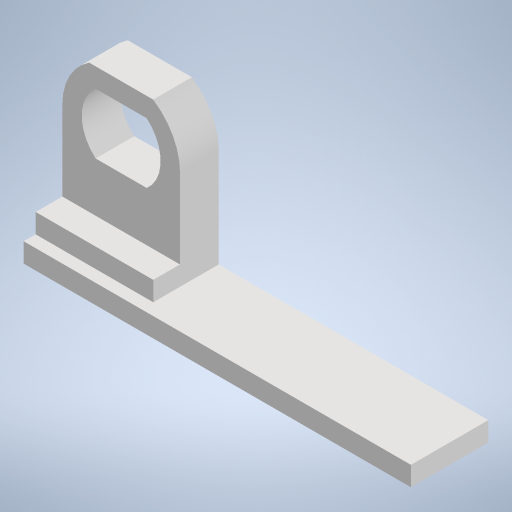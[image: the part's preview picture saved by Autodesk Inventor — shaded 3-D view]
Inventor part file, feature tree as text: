
AUTODESK INVENTOR PART (.ipt)
format: ipt  version: 2023 (Build 270158000, 158)  size: 253,440 bytes
history: native  units: mm
features: extrude x3, plane x2, sketch x1
ambient origin geometry x8: Origin, YZ Plane, XZ Plane, XY Plane, X Axis, Y Axis, Z Axis, Center Point
bodies: Solid1 (feature_tree)
feature tree (6):
  plane  "Work Plane1"
  sketch  "Sketch2"  dims[d5=0.3mm d6=5.0mm d7=30.6mm d10=10.0mm d11=0.0mm d12=10.0mm d13=0.0mm d14=6.9mm d15=0.0mm d16=100.0mm d17=10.0mm d18=0.0mm]
  extrude  "Extrusion1"  Depth=5.0mm
  plane  "Work Plane2"
  extrude  "Extrusion2"  Depth=10.0mm
  extrude  "Extrusion3"  Depth=10.0mm TaperAngle=0.0deg
